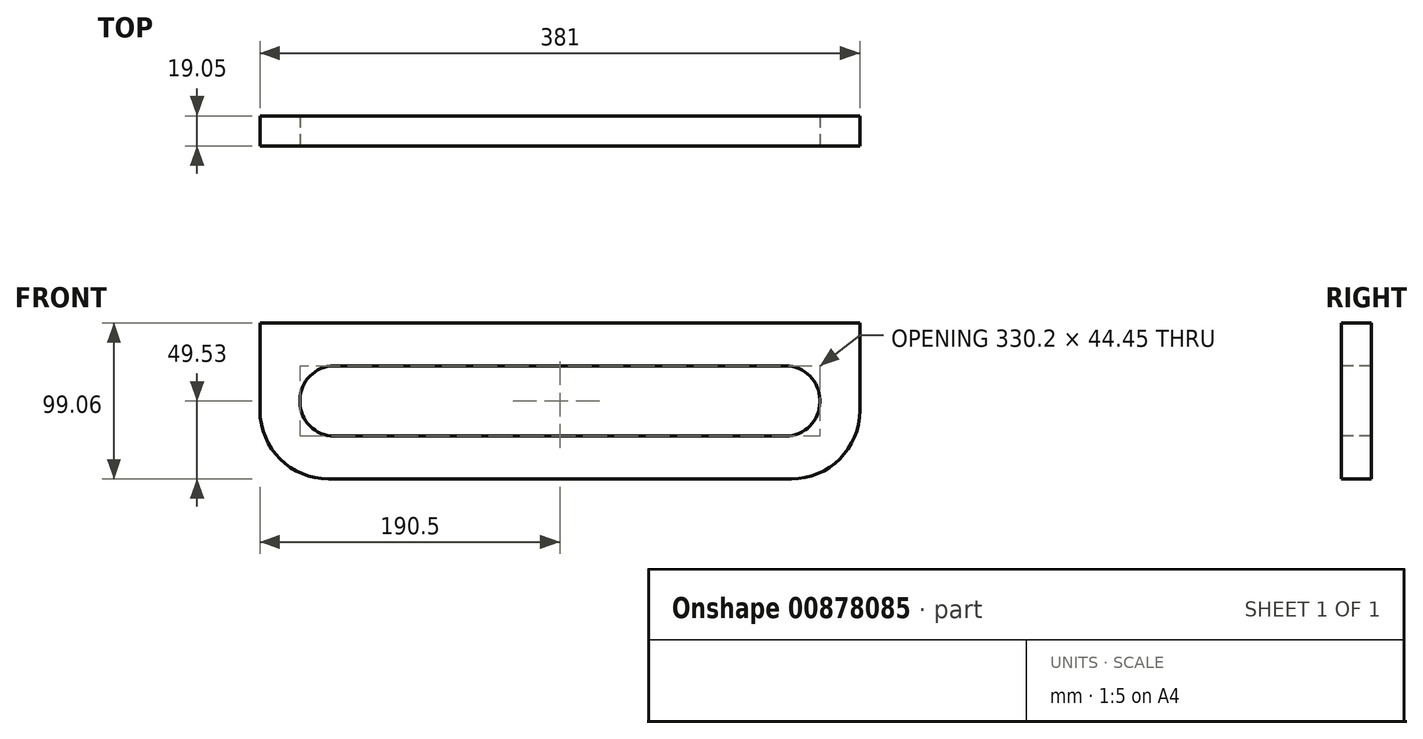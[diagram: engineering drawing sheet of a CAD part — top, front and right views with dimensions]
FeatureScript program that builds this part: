
annotation { "Feature Type Name" : "Feature", "Feature Type Description" : "" }
export const myFeature = defineFeature(function(context is Context, id is Id, definition is map)
    precondition{}
    {
        {
            var Q0;
            Q0=qCreatedBy(makeId("Front.planeOp"),FACE);
            var sketch = newSketch(context, id + "F0", { "sketchPlane" : qUnion([Q0])});
            skLineSegment(sketch, "E0", {"start": v(0, 0) * mm, "end": v(381, 0) * mm});
            skLineSegment(sketch, "E1", {"start": v(0, 0) * mm, "end": v(0, -99.06) * mm});
            skLineSegment(sketch, "E2", {"start": v(0, -99.06) * mm, "end": v(381, -99.06) * mm});
            skLineSegment(sketch, "E3", {"start": v(381, -99.06) * mm, "end": v(381, 0) * mm});
            skSolve(sketch);
        }
        {
            var Q0;
            Q0=makeQuery(id+"F0.imprint","IMPRINT",FACE,{"disambiguationData":[TD([[makeQuery(id+"F0.imprint","IMPRINT",EDGE,{"derivedFrom":sQuery(id+"F0.wireOp",EDGE,"E0")}),-1.0]])]});
            extrude(context, id + "F1", {"entities" : qUnion([Q0]), "depth" : 19.05 * mm, "offsetDistance" : 25.4 * mm});
        }
        {
            var Q0;
            Q0=makeQuery(id+"F1.opExtrude","SWEPT_EDGE",EDGE,{"disambiguationData":[OSD([sQuery(id+"F0.wireOp",EDGE,"E1"),sQuery(id+"F0.wireOp",EDGE,"E2")])]});
            var Q1;
            Q1=makeQuery(id+"F1.opExtrude","SWEPT_EDGE",EDGE,{"disambiguationData":[OSD([sQuery(id+"F0.wireOp",EDGE,"E2"),sQuery(id+"F0.wireOp",EDGE,"E3")])]});
            fillet(context, id + "F2", {"entities" : qUnion([Q0, Q1]), "radius" : 43.54 * mm, "tangentPropagation" : true, "allowEdgeOverflow" : false});
        }
        {
            var Q0;
            Q0=makeQuery(id+"F1.opExtrude","CAP_FACE",FACE,{"disambiguationData":[OSD([sQuery(id+"F0.wireOp",EDGE,"E0"),sQuery(id+"F0.wireOp",EDGE,"E1"),sQuery(id+"F0.wireOp",EDGE,"E2"),sQuery(id+"F0.wireOp",EDGE,"E3")])],"isStart":false});
            var sketch = newSketch(context, id + "F3", { "sketchPlane" : qUnion([Q0])});
            skLineSegment(sketch, "E4.bottom", {"start": v(25.4, -27.3) * mm, "end": v(355.6, -27.3) * mm});
            skLineSegment(sketch, "E4.top", {"start": v(25.4, -71.76) * mm, "end": v(355.6, -71.76) * mm});
            skLineSegment(sketch, "E4.left", {"start": v(25.4, -27.3) * mm, "end": v(25.4, -71.76) * mm});
            skLineSegment(sketch, "E4.right", {"start": v(355.6, -27.3) * mm, "end": v(355.6, -71.76) * mm});
            skLineSegment(sketch, "E5", {"start": v(25.4, -49.53) * mm, "end": v(0, -49.53) * mm, "construction": true});
            skLineSegment(sketch, "E6", {"start": v(355.6, -49.53) * mm, "end": v(381, -49.53) * mm, "construction": true});
            skLineSegment(sketch, "E7", {"start": v(190.5, -27.3) * mm, "end": v(190.5, 0) * mm, "construction": true});
            skLineSegment(sketch, "E8", {"start": v(190.5, -71.76) * mm, "end": v(190.5, -99.06) * mm, "construction": true});
            skSolve(sketch);
        }
        {
            var Q0;
            Q0=makeQuery(id+"F3.imprint","IMPRINT",FACE,{"disambiguationData":[TD([[makeQuery(id+"F3.imprint","IMPRINT",EDGE,{"derivedFrom":sQuery(id+"F3.wireOp",EDGE,"E4.bottom")}),-1.0]])]});
            extrude(context, id + "F4", {"entities" : qUnion([Q0]), "operationType" : NewBodyOperationType.REMOVE, "endBound" : BoundingType.THROUGH_ALL, "oppositeDirection" : true, "depth" : 25.4 * mm, "offsetDistance" : 25.4 * mm});
        }
        {
            var Q0;
            Q0=makeQuery(id+"F4.boolean.opBoolean","COPY",EDGE,{"derivedFrom":makeQuery(id+"F4.opExtrude","SWEPT_EDGE",EDGE,{"disambiguationData":[OSD([sQuery(id+"F3.wireOp",EDGE,"E4.top"),sQuery(id+"F3.wireOp",EDGE,"E4.left")])]})});
            var Q1;
            Q1=makeQuery(id+"F4.boolean.opBoolean","COPY",EDGE,{"derivedFrom":makeQuery(id+"F4.opExtrude","SWEPT_EDGE",EDGE,{"disambiguationData":[OSD([sQuery(id+"F3.wireOp",EDGE,"E4.bottom"),sQuery(id+"F3.wireOp",EDGE,"E4.left")])]})});
            var Q2;
            Q2=makeQuery(id+"F4.boolean.opBoolean","COPY",EDGE,{"derivedFrom":makeQuery(id+"F4.opExtrude","SWEPT_EDGE",EDGE,{"disambiguationData":[OSD([sQuery(id+"F3.wireOp",EDGE,"E4.bottom"),sQuery(id+"F3.wireOp",EDGE,"E4.right")])]})});
            var Q3;
            Q3=makeQuery(id+"F4.boolean.opBoolean","COPY",EDGE,{"derivedFrom":makeQuery(id+"F4.opExtrude","SWEPT_EDGE",EDGE,{"disambiguationData":[OSD([sQuery(id+"F3.wireOp",EDGE,"E4.top"),sQuery(id+"F3.wireOp",EDGE,"E4.right")])]})});
            fillet(context, id + "F5", {"entities" : qUnion([Q0, Q1, Q2, Q3]), "radius" : 21.59 * mm, "tangentPropagation" : true, "allowEdgeOverflow" : false});
        }
    });
